FCSTD DOCUMENT  (FreeCAD 0.20R29177 (Git))
Label: Tail
License: All rights reserved
LicenseURL: http://en.wikipedia.org/wiki/All_rights_reserved
objects: App::Link×2, Spreadsheet::Sheet×1, App::Part×1
EXTERNAL_REF file=../Master_of_Puppets.FCStd obj=HighEndStop
EXTERNAL_REF file=../Master_of_Puppets.FCStd obj=Tail
EXTERNAL_REF file=Tail_Assembly_BoomVane.FCStd obj=Part001
EXTERNAL_REF file=Hinge/Outer/Tail_Hinge_Outer.FCStd obj=Part

FEATURE [Spreadsheet::Sheet] Spreadsheet
  cells = A1=Inputs; A2=TailPlacement (TailBoomVaneAssembly); B2(TailPlacement)==Master_of_Puppets#HighEndStop.TailPlacement; A3=OuterTailHingePlacement; B3(OuterTailHingePlacement)==Master_of_Puppets#Tail.OuterTailHingePlacement; A4=FurlAxis; B4(FurlAxis)==Master_of_Puppets#HighEndStop.FurlAxis
FEATURE [App::Link] Link  label="Assembly_BoomVane"
  LinkPlacement = pos=(126.484,5.6656,173.663) rot=(0,0,1;0.261799rad)
  LinkTransform = true
  LinkedObject = -> <external Tail_Assembly_BoomVane.FCStd>#Part001
  Placement = pos=(126.484,5.6656,173.663) rot=(0,0,1;0.261799rad)
  expr: LinkPlacement = Spreadsheet.TailPlacement
FEATURE [App::Link] Link001  label="Hinge_Outer"
  LinkPlacement = pos=(76.7329,0,98.7939) rot=(0,1,0;0.349066rad)
  LinkedObject = -> <external Hinge/Outer/Tail_Hinge_Outer.FCStd>#Part
  Placement = pos=(76.7329,0,98.7939) rot=(0,1,0;0.349066rad)
  expr: LinkPlacement = Spreadsheet.OuterTailHingePlacement
FEATURE [App::Part] Part  label="Tail"
  Group = -> [Link001,Link]
  Origin = -> Origin
  expr: .Placement.Rotation.Axis = Spreadsheet.FurlAxis

RESOLVED EXTERNAL PARTS (link-assembly join: the EXTERNAL_REF files above that resolve inside this repo's crawl, each included once):
---- part ../Master_of_Puppets.FCStd = doc fcstd_6404554055c4 (61625 chars; too large to inline — full recipe in that document) ----
---- part Hinge/Outer/Tail_Hinge_Outer.FCStd = doc fcstd_5bdfc7f9d256 ----
FCSTD DOCUMENT  (FreeCAD 1.0R39109 (Git))
Label: Tail_Hinge_Outer
License: All rights reserved
LicenseURL: http://en.wikipedia.org/wiki/All_rights_reserved
objects: App::Link×3, Spreadsheet::Sheet×1, Part::Cylinder×1, Part::Cut×1, App::Part×1
note: 2 computed .brp shape members not serialized (recipe doc carries the construction recipe); baked Part::Feature solids carry a one-line shape summary decoded from their .brp
EXTERNAL_REF file=Tail_Hinge_Outer_Pipe.FCStd obj=Tube
EXTERNAL_REF file=Tail_Hinge_Outer_Pipe_Cover.FCStd obj=PadBody
EXTERNAL_REF file=../../../Master_of_Puppets.FCStd obj=Alternator
EXTERNAL_REF file=../../../Master_of_Puppets.FCStd obj=HighEndStop
EXTERNAL_REF file=../../../Master_of_Puppets.FCStd obj=LowEndStop
EXTERNAL_REF file=../../../Master_of_Puppets.FCStd obj=Spreadsheet
EXTERNAL_REF file=../../../Master_of_Puppets.FCStd obj=Tail
EXTERNAL_REF file=../../Stops/Tail_Stop_LowEnd.FCStd obj=PocketBody

FEATURE [App::Link] Link  label="Pipe"
  LinkedObject = -> <external Tail_Hinge_Outer_Pipe.FCStd>#Tube
FEATURE [App::Link] Link001  label="Outer_Pipe_Cover"
  LinkPlacement = pos=(0,0,225.987) rot=(0,0,1;0rad)
  LinkedObject = -> <external Tail_Hinge_Outer_Pipe_Cover.FCStd>#PadBody
  Placement = pos=(0,0,225.987) rot=(0,0,1;0rad)
  expr: .Placement.Base.z = Spreadsheet.HingeOuterPipeCoverZ
FEATURE [Spreadsheet::Sheet] Spreadsheet
  cells = A1='Inputs; A2='HingeOuterPipeLength; B2(HingeOuterPipeLength)==Master_of_Puppets#Tail.HingeOuterPipeLength; A3='FlatMetalThickness; B3(FlatMetalThickness)==Master_of_Puppets#Spreadsheet.FlatMetalThickness; A4='TailBoomTriangularBraceWidth; B4(TailBoomTriangularBraceWidth)==Master_of_Puppets#Tail.TailBoomTriangularBraceWidth; A5='LowEndStopPlacement; B5(LowEndStopPlacement)==Master_of_Puppets#LowEndStop.LowEndStopPlacement; A6='YawPipeRadius; B6(YawPipeRadius)==Master_of_Puppets#Alternator.YawPipeRadius; A7='YawPipeLength; B7(YawPipeLength)==Master_of_Puppets#HighEndStop.YawPipeLength; A8='OuterTailHingePlacement; B8(OuterTailHingePlacement)==Master_of_Puppets#Tail.OuterTailHingePlacement; A9='TailAssemblyPlacement; B9(TailAssemblyPlacement)==Master_of_Puppets#HighEndStop.TailAssemblyPlacement; A10='Placement; A11='HingeOuterPipeCoverZ; B11(HingeOuterPipeCoverZ)==HingeOuterPipeLength; A12='YawBearingCylinderPlacement; B12(YawBearingCylinderPlacement)==minvert(OuterTailHingePlacement) * minvert(TailAssemblyPlacement)
FEATURE [App::Link] Link002  label="Stop_LowEnd"
  LinkPlacement = pos=(0,0,155.983) rot=(0,0,-1;1.29045rad)
  LinkedObject = -> <external ../../Stops/Tail_Stop_LowEnd.FCStd>#PocketBody
  Placement = pos=(0,0,155.983) rot=(0,0,-1;1.29045rad)
  expr: Placement = Spreadsheet.LowEndStopPlacement
FEATURE [Part::Cylinder] Cylinder  label="YawBearing_Cylinder"
  Angle = 360
  AttacherType = Attacher::AttachEngine3D
  FirstAngle = 0
  Height = 405
  Placement = pos=(-79.4354,1.24e-14,-150.518) rot=(-0.130416,-0.04112,0.990606;2.53612rad)
  Radius = 44.45
  SecondAngle = 0
  expr: Height = Spreadsheet.YawPipeLength
  expr: Placement = Spreadsheet.YawBearingCylinderPlacement
  expr: Radius = Spreadsheet.YawPipeRadius
FEATURE [Part::Cut] Cut  label="Tail_Stop_LowEnd"
  Base = -> Link002
  Openafpm_Flat = true
  Tool = -> Cylinder
FEATURE [App::Part] Part  label="Tail_Hinge_Outer"
  Group = -> [Link,Link001,Link002,Cylinder,Cut]
  Origin = -> Origin
---- part Tail_Assembly_BoomVane.FCStd = doc fcstd_f393e86370a3 ----
FCSTD DOCUMENT  (FreeCAD 0.20R29177 (Git))
Label: Tail_Assembly_BoomVane
License: All rights reserved
LicenseURL: http://en.wikipedia.org/wiki/All_rights_reserved
objects: App::Link×5, Spreadsheet::Sheet×1, Part::Mirroring×1, Part::Cylinder×1, Part::Cut×1, App::Part×1
note: 3 computed .brp shape members not serialized (recipe doc carries the construction recipe); baked Part::Feature solids carry a one-line shape summary decoded from their .brp
EXTERNAL_REF file=Boom/Tail_Boom_Support.FCStd obj=PadBody
EXTERNAL_REF file=../Master_of_Puppets.FCStd obj=HighEndStop
EXTERNAL_REF file=../Master_of_Puppets.FCStd obj=Spreadsheet
EXTERNAL_REF file=../Master_of_Puppets.FCStd obj=Tail
EXTERNAL_REF file=Vane/Tail_Vane_Bracket.FCStd obj=Part
EXTERNAL_REF file=Boom/Tail_Boom_Pipe.FCStd obj=Tube
EXTERNAL_REF file=Vane/Tail_Vane.FCStd obj=Fillet001Body
EXTERNAL_REF file=Stops/Tail_Stop_HighEnd.FCStd obj=PadBody

FEATURE [App::Link] Link001  label="Boom_Support"
  LinkPlacement = pos=(24.15,0,0) rot=(0,0,1;0.087712rad)
  LinkTransform = true
  LinkedObject = -> <external Boom/Tail_Boom_Support.FCStd>#PadBody
  Placement = pos=(24.15,0,0) rot=(0,0,1;0.087712rad)
  expr: .LinkPlacement.Base.x = Spreadsheet.TailBoomTriangularBraceX
  expr: .LinkPlacement.Base.y = Spreadsheet.TailBoomTriangularBraceY
  expr: .LinkPlacement.Base.z = Spreadsheet.TailBoomTriangularBraceZ
  expr: .LinkPlacement.Rotation.Angle = Spreadsheet.TailBoomTriangularBraceZAxisAngle
FEATURE [Spreadsheet::Sheet] Spreadsheet
  cells = A1=Inputs; A2=BoomPipeDiameter; B2(BoomPipeDiameter)==Master_of_Puppets#Spreadsheet.BoomPipeDiameter; A3=FlatMetalThickness; B3(FlatMetalThickness)==Master_of_Puppets#Spreadsheet.FlatMetalThickness; A4=BracketThickness; B4(BracketThickness)==Master_of_Puppets#Spreadsheet.BracketThickness; A5=BoomLength; B5(BoomLength)==Master_of_Puppets#Spreadsheet.BoomLength; A6=BracketLength; B6(BracketLength)==Master_of_Puppets#Spreadsheet.BracketLength; A7=BracketWidth; B7(BracketWidth)==Master_of_Puppets#Spreadsheet.BracketWidth; A8=VerticalPlaneAngle; B8(VerticalPlaneAngle)==Master_of_Puppets#Spreadsheet.VerticalPlaneAngle; A9=VaneBracketAngle; B9(VaneBracketAngle)==Master_of_Puppets#Tail.VaneBracketAngle; A10=TailBoomTriangularBraceZAxisAngle; B10(TailBoomTriangularBraceZAxisAngle)==Master_of_Puppets#Tail.TailBoomTriangularBraceZAxisAngle; A11=VaneThickness; B11(VaneThickness)==Master_of_Puppets#Spreadsheet.VaneThickness; A12=HingeOuterPipeRadius; B12(HingeOuterPipeRadius)==Master_of_Puppets#Tail.HingeOuterPipeRadius; A13=HingeOuterPipeLength; B13(HingeOuterPipeLength)==Master_of_Puppets#Tail.HingeOuterPipeLength; A14=OuterTailHingePlacement; B14(OuterTailHingePlacement)==Master_of_Puppets#Tail.OuterTailHingePlacement; A15=TailPlacement (TailBoomVaneAssembly); B15(TailPlacement)==Master_of_Puppets#HighEndStop.TailPlacement; A16=Calculated; A17=BoomPipeRadius; B17(BoomPipeRadius)==BoomPipeDiameter / 2; A18=Placement; A19=TailAssemblyBoomVane; B19=HighEndStopPlacement; A20(TailAssemblyBoomVanePlacement)==create(<<placement>>; create(<<vector>>); create(<<rotation>>; create(<<vector>>; 0; 1; 0); 90)); B20(HighEndStopPlacement)==Master_of_Puppets#HighEndStop.HighEndStopPlacement; A21=TailBoomTriangularBrace; A22=X; B22=Y; C22=Z; A23(TailBoomTriangularBraceX)==BoomPipeRadius; B23(TailBoomTriangularBraceY)=0; C23(TailBoomTriangularBraceZ)=0; A24=TopTailVaneBracket; A25=BracketWidthTriangleSide; B25=TailVaneBracketXOffset; C25=BracketLengthTriangleSide; A26(BracketWidthTriangleSide)==BracketWidth * cos(VaneBracketAngle); B26(TailVaneBracketXOffset)==BoomPipeRadius + BracketWidthTriangleSide; C26(BracketLengthTriangleSide)==BracketLength * cos(VaneBracketAngle); A27=Opposite; B27=BracketEndAdajcent; C27=BracketHypotenuse; A28(Opposite)==sin(VaneBracketAngle) * BracketLength; B28(BracketEndAdajcent)==cos(90 - VaneBracketAngle) * BracketWidth; C28(BracketHypotenuse)==BracketWidth / sin(VaneBracketAngle); A29=X; B29=Y; C29=Z; A30(TopTailVaneBracketX)==(Opposite + 2 * BoomPipeRadius - TailVaneBracketXOffset) * -1; B30(TopTailVaneBracketY)==-BracketThickness / 2; C30(TopTailVaneBracketZ)==BoomLength + BracketLengthTriangleSide + BracketEndAdajcent - BracketHypotenuse; B31=TopTailVaneBracketY Duplicated in Tail; A32=Angle; A33(TopTailVaneBracketAngle)==-VaneBracketAngle; A34=TailVane; A35=X; B35=Y; C35=Z; A36(TailVaneX)=0; B36(TailVaneY)==TopTailVaneBracketY - VaneThickness; C36(TailVaneZ)==BoomLength; A37=HingeOuterCylinder; A38(HingeOuterCylinderPlacement)==minvert(TailAssemblyBoomVanePlacement) * minvert(TailPlacement) * OuterTailHingePlacement
FEATURE [App::Link] Link004  label="Vane_Bracket_Top"
  LinkPlacement = pos=(-215.069,-2.5,1190.92) rot=(0,1,0;-0.785398rad)
  LinkTransform = true
  LinkedObject = -> <external Vane/Tail_Vane_Bracket.FCStd>#Part
  Placement = pos=(-215.069,-2.5,1190.92) rot=(0,1,0;-0.785398rad)
  expr: .LinkPlacement.Base.x = Spreadsheet.TopTailVaneBracketX
  expr: .LinkPlacement.Base.y = Spreadsheet.TopTailVaneBracketY
  expr: .LinkPlacement.Base.z = Spreadsheet.TopTailVaneBracketZ
  expr: .LinkPlacement.Rotation.Angle = Spreadsheet.TopTailVaneBracketAngle
FEATURE [App::Link] Link  label="Boom_Pipe"
  LinkedObject = -> <external Boom/Tail_Boom_Pipe.FCStd>#Tube
FEATURE [Part::Mirroring] mirror  label="Vane_Bracket_Bottom"
  Base = (0.000366211,-6.84779,1074.31)
  Normal = (1,-0.000576858,0.000545144)
  Source = -> Link004
FEATURE [App::Link] Link005  label="Vane"
  LinkPlacement = pos=(0,-8.5,1000) rot=(-0.57735,-0.57735,-0.57735;2.0944rad)
  LinkedObject = -> <external Vane/Tail_Vane.FCStd>#Fillet001Body
  Placement = pos=(0,-8.5,1000) rot=(-0.57735,-0.57735,-0.57735;2.0944rad)
  expr: .Placement.Base.x = Spreadsheet.TailVaneX
  expr: .Placement.Base.y = Spreadsheet.TailVaneY
  expr: .Placement.Base.z = Spreadsheet.TailVaneZ
FEATURE [Part::Cylinder] Cylinder  label="Hinge_Outer_Cylinder"
  Angle = 360
  AttacherType = Attacher::AttachEngine3D
  FirstAngle = 0
  Height = 126.076
  Placement = pos=(74.8689,7.40405,-49.5225) rot=(0.183254,-0.974655,-0.128316;1.24596rad)
  Radius = 30.15
  SecondAngle = 0
  expr: Height = Spreadsheet.HingeOuterPipeLength
  expr: Placement = Spreadsheet.HingeOuterCylinderPlacement
  expr: Radius = Spreadsheet.HingeOuterPipeRadius
FEATURE [App::Link] Link002  label="Stop_HighEnd_Link"
  LinkPlacement = pos=(5,24.15,0) rot=(0,1,0;-1.5708rad)
  LinkedObject = -> <external Stops/Tail_Stop_HighEnd.FCStd>#PadBody
  Placement = pos=(5,24.15,0) rot=(0,1,0;-1.5708rad)
  expr: Placement = Spreadsheet.HighEndStopPlacement
FEATURE [Part::Cut] Cut  label="Tail_Stop_HighEnd"
  Base = -> Link002
  Openafpm_Flat = true
  Tool = -> Cylinder
FEATURE [App::Part] Part001  label="Tail_Assembly_BoomVane"
  Group = -> [Link,Link001,Link004,mirror,Link005,Link002,Cylinder,Cut]
  Origin = -> Origin001
  Placement = pos=(0,0,0) rot=(0,1,0;1.5708rad)
